# Revit family: KEUCO_59580010100
name_source: partatom
category: Sonderausstattung
revit_build: Autodesk Revit 2016 (Build: 20150220_1215(x64)
units: mm (PartAtom-declared; Revit-internal decimal feet)

## family parameters
Arbeitsebenenbasiert = Nein
Beim Laden mit Abzugskörper schneiden = Nein
Bemaßung runder Anschluss = Durchmesser verwenden
Gemeinsam genutzt = Nein
Immer vertikal = Ja
OmniClass-Nummer = 23.45.00.00
Raumberechnungspunkt = Nein
Teiletyp = Normal

## types (1)
- 59580010100
    Artikelnummer = 59580010100
    Ausschreibungstext = KEUCO Handbrause 59580010100
Hochglanzverchromte Handbrause 
mit Normalstrahl und ECO AIR Funktion
auch für Durchlauferhitzer geeignet
    Beschreibung = mit Normalstrahl
mit ECO AIR Funktion
Durchflussmenge 11 l/min.
für Durchlauferhitzer geeignet
    Gewicht = 1.408
    Hersteller = KEUCO
    Kategorie = ARM
    Preisgruppe = 1
    Serie = IXMO
    Stange Länge = 850 mm  [stored 2.78871 ft]
    URL = https://www.keuco.com
    Verwendung = DU / WA

note: [stored X ft] marks values corroborated as IEEE doubles in the binary element streams (Revit-internal decimal feet)

## geometry (parser evidence)
native form markers: Blend x2, Sweep x3
no freeform markers — native parametric forms only
